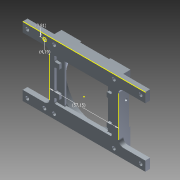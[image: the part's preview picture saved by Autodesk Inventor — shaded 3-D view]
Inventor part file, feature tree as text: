
AUTODESK INVENTOR PART (.ipt)
format: ipt  version: 2015 (Build 190159000, 159)  size: 295,936 bytes
history: native  units: in
note: dims shown in document units (in); Inventor stores cm internally (conversion verified against a paired STEP export)
features: sketch x2, other x1, extrude x1, imported_body x1, projected_geometry x1
ambient origin geometry x8: Origin, YZ Plane, XZ Plane, XY Plane, X Axis, Y Axis, Z Axis, Center Point
bodies: Body1 (feature_tree)
feature tree (6):
  other  "Sensormount_CMV12000-H1"
  extrude  "Extrusion1"  Depth=0.315in
  sketch  "Sketch2"  dims[d2=0.1181in d3=0.315in d4=0.3937in d5=0.0in d6=0.165in d7=0.15in d8=2.25in]
  imported_body  "Base1"
  sketch  "Sketch1"  dims[d0=0.1181in d1=0.315in]
  projected_geometry  "Projected Loop1"
